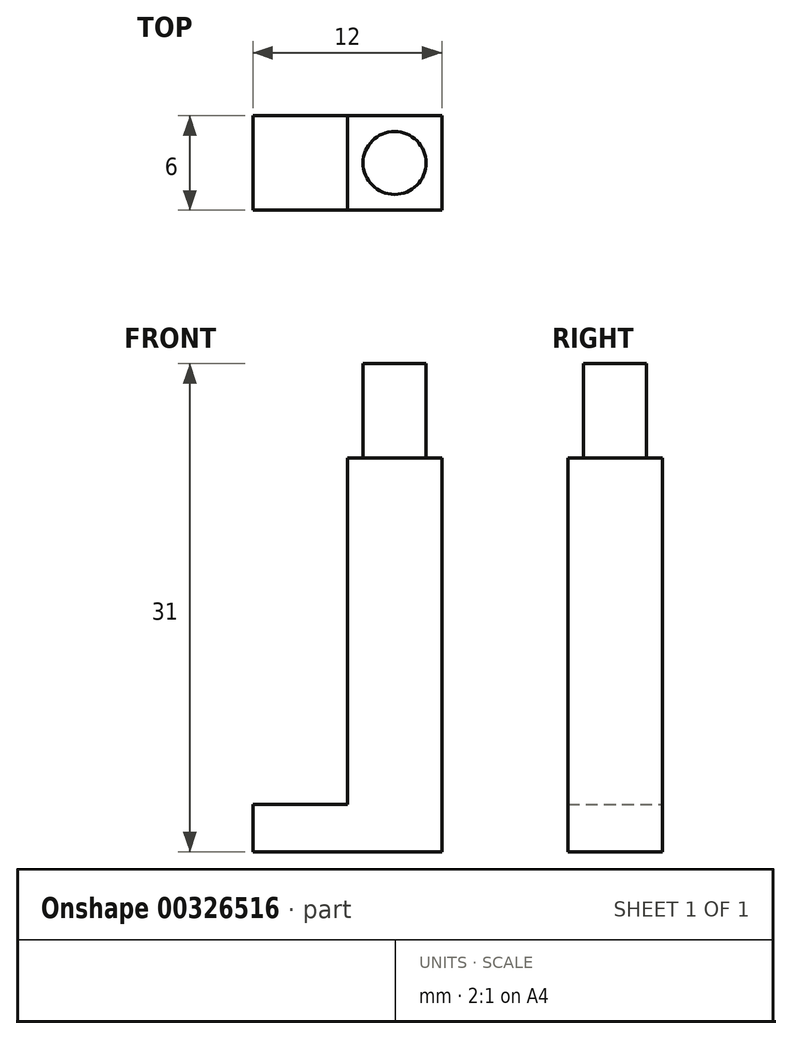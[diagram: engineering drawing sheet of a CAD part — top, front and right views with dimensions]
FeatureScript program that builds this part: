
annotation { "Feature Type Name" : "Feature", "Feature Type Description" : "" }
export const myFeature = defineFeature(function(context is Context, id is Id, definition is map)
    precondition{}
    {
        {
            var Q0;
            Q0=qCreatedBy(makeId("Front.planeOp"),FACE);
            var sketch = newSketch(context, id + "F0", { "sketchPlane" : qUnion([Q0])});
            skLineSegment(sketch, "E0.bottom", {"start": v(-3, 12.5) * mm, "end": v(3, 12.5) * mm});
            skLineSegment(sketch, "E0.top", {"start": v(-3, -12.5) * mm, "end": v(3, -12.5) * mm});
            skLineSegment(sketch, "E0.left", {"start": v(-3, 12.5) * mm, "end": v(-3, -9.5) * mm});
            skLineSegment(sketch, "E0.right", {"start": v(3, 12.5) * mm, "end": v(3, -12.5) * mm});
            skPoint(sketch, "E0.middle", {"position": v(0, 0) * mm});
            skLineSegment(sketch, "E1.bottom", {"start": v(-3, -12.5) * mm, "end": v(-9, -12.5) * mm});
            skLineSegment(sketch, "E1.top", {"start": v(-3, -9.5) * mm, "end": v(-9, -9.5) * mm});
            skLineSegment(sketch, "E1.right", {"start": v(-9, -12.5) * mm, "end": v(-9, -9.5) * mm});
            skSolve(sketch);
        }
        {
            var Q0;
            Q0=makeQuery(id+"F0.imprint","IMPRINT",FACE,{"disambiguationData":[TD([[makeQuery(id+"F0.imprint","IMPRINT",EDGE,{"derivedFrom":sQuery(id+"F0.wireOp",EDGE,"E0.bottom")}),-1.0]])]});
            extrude(context, id + "F1", {"entities" : qUnion([Q0]), "depth" : 6 * mm});
        }
        {
            var Q0;
            Q0=makeQuery(id+"F1.opExtrude","SWEPT_FACE",FACE,{"disambiguationData":[OSD([sQuery(id+"F0.wireOp",EDGE,"E0.bottom")])]});
            var sketch = newSketch(context, id + "F2", { "sketchPlane" : qUnion([Q0])});
            skCircle(sketch, "E2", {"center": v(0, -3) * mm, "radius": 2 * mm});
            skSolve(sketch);
        }
        {
            var Q0;
            Q0=makeQuery(id+"F2.imprint","IMPRINT",FACE,{"disambiguationData":[TD([[makeQuery(id+"F2.imprint","IMPRINT",EDGE,{"derivedFrom":sQuery(id+"F2.wireOp",EDGE,"E2")}),1.0]])]});
            extrude(context, id + "F3", {"entities" : qUnion([Q0]), "operationType" : NewBodyOperationType.ADD, "depth" : 6 * mm});
        }
    });
